# Revit family: Product Jnr
name_source: partatom
category: Plumbing Fixtures
units: mm (PartAtom-declared; Revit-internal decimal feet)

## family parameters
Always vertical = Yes
Cut with Voids When Loaded = No
Part Type = Normal
Room Calculation Point = No
Round Connector Dimension = Use Diameter
Shared = No
Work Plane-Based = Yes

## types (1)
- Hibiscus Elite Cc
    Assembly Code = D2010110
    CW Connection = Yes
    CW Connection Radius = 32 mm  [stored 0.104987 ft]
    Default Elevation = 1219 mm
    Finish = Vitreous China-Vaal-White
    HW Connection = No
    Manufacturer = Vaal Sanitaryware
    Model = Hibiscus Close Coupled Suite
    Offset = 10 mm  [stored 0.0328084 ft]
    Seat Finish = Plastic-Vaal-White
    URL = http://www.vaalsan.co.za
    Vent Connection = No
    Waste Connection = Yes
    Waste Connection Radius = 55 mm  [stored 0.180446 ft]

note: [stored X ft] marks values corroborated as IEEE doubles in the binary element streams (Revit-internal decimal feet)

## geometry (parser evidence)
native form markers: Sweep x2
no freeform markers — native parametric forms only
